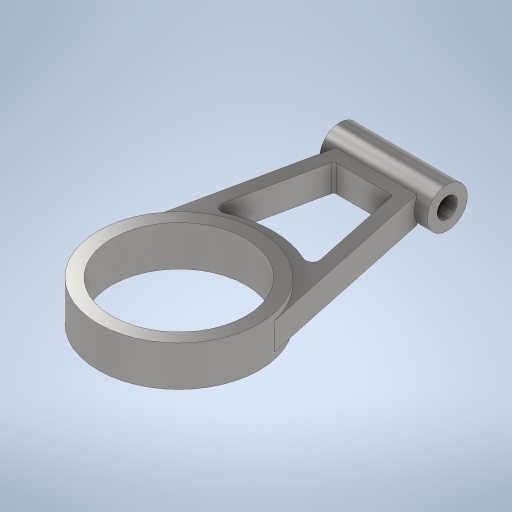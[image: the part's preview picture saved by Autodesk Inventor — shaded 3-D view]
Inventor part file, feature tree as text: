
AUTODESK INVENTOR PART (.ipt)
format: ipt  version: 2024 (Build 280153000, 153)  size: 321,024 bytes
history: native  units: mm
features: extrude x5, sketch x4, fillet x2, plane x1, projected_geometry x1
ambient origin geometry x8: Origin, YZ Plane, XZ Plane, XY Plane, X Axis, Y Axis, Z Axis, Center Point
bodies: Volumenkörper1 (feature_tree)
feature tree (13):
  sketch  "Skizze1"  dims[d0=120.0mm d1=4.18879mm]
  extrude  "Extrusion1"  Depth=4.18879mm
  extrude  "Extrusion2"  Depth=30.0mm TaperAngle=0.0deg
  extrude  "Extrusion3"  Depth=20.0mm
  plane  "Arbeitsebene1"
  extrude  "Extrusion4"  TaperAngle=0.0deg  [1 undecoded]
  extrude  "Extrusion5"  Depth=30.0mm
  fillet  "Rundung1"  Radius=160.0mm
  fillet  "Rundung2"  Radius=15.0mm
  sketch  "Skizze2"  dims[d2=60.0mm d3=30.0mm d4=0.0mm]
  sketch  "Skizze3"  dims[d5=20.0mm d6=0.0mm d7=100.0mm]
  projected_geometry  "Projizierte Kontur1"
  sketch  "Skizze4"  dims[d8=20.0mm d9=0.0mm d10=0.0mm d11=30.0mm d12=160.0mm d13=15.0mm d14=80.0mm d15=0.0mm d16=10.0mm d17=10.0mm d18=70.0mm d19=80.0mm d20=0.0mm d21=5.0mm d22=2.0mm]
note: 1 required parameter value undecoded (feature->parameter linkage not recoverable at this tier; creation-order binding heuristic only, values carry confidence <= 0.55)
